# Revit family: Showerhead-Waterworks-Flyte-Arm_Flange
name_source: partatom
category: Plumbing Fixtures
revit_build: Autodesk Revit MEP 2014 (Build: 20140709_2115(x64)
units: mm (PartAtom-declared; Revit-internal decimal feet)

## types (4) — shared parameters
ADA Compliant = No
Anti-scald Protection = No
Assembly Code = D2010710
CW Connection = Yes
Certification IAPMO = Yes
Certification State of MA = Yes
Certification cUPC = Yes
Code Compliance = Code # FLSH01: Complies with ASME A112.18.1/CSA B125.1, ASTM E 1621-05.  Certified with IAPMO, cUPC & State of MA
Depth = 0' - 9 5/8"
Fittings Hole Diameter = 0' - 1"
HW Connection = Yes
Height = 0' - 3 5/16"
Hot Limit Safety Stop = No
Inlet Connection Diameter = 0' - 0 1/2"
Keynote = 22 40 00
Length = 0' - 2 3/8"
Manufacturer = Waterworks
Model = FLSH01
Pressure = 45.00 psi
Product Documentation Link = http://assets.waterworks.com
Product Page URL = http://www.waterworks.com
URL = http://www.waterworks.com
Vent Connection = No
Version = 2014 - v1.0a
Warranty = http://www.waterworks.com
Waste Connection = No
Water Connector = Water - Male NPT
Water Pressure = Max: 85psi / Min: 20psi / Recommended: 45psi
‌Installation Requirements or Notes = Shower arms can be partnered with a variety of shower heads (sold separately): 6'' rain head, 4 1/2'' shower rose, or 2 3/4'' shower head with adjustable spray
zero-valued in all types: CWFU, HWFU, WFU

## per-type parameters (varying)
| type | Constraint | Default Elevation | Description | Finish | Model SKU | Product Name |
| Chrome | 1 | 6' - 6" | Shower Arm and Flange in Chrome | Metal - Waterworks - Chrome | 05-75929-52781 | Flyte Shower Arm and Flange in Chrome |
| Graphite | 2 | 2' - 10" | Shower Arm and Flange in Graphite | Metal - Waterworks - Graphite | 05-13380-83807 | Flyte Shower Arm and Flange in Graphite |
| Nickel | 3 | 2' - 10" | Shower Arm and Flange in Nickel | Metal - Waterworks - Nickel | 05-63769-47825 | Flyte Shower Arm and Flange in Nickel |
| Unlacquered Brass | 4 | 2' - 10" | Shower Arm and Flange in Unlacquered Brass | Metal - Waterworks - Unlacquered Brass | 05-35062-63247 | Flyte Shower Arm and Flange in Unlacquered Brass |

## geometry (parser evidence)
native form markers: Sweep x6
no freeform markers — native parametric forms only
